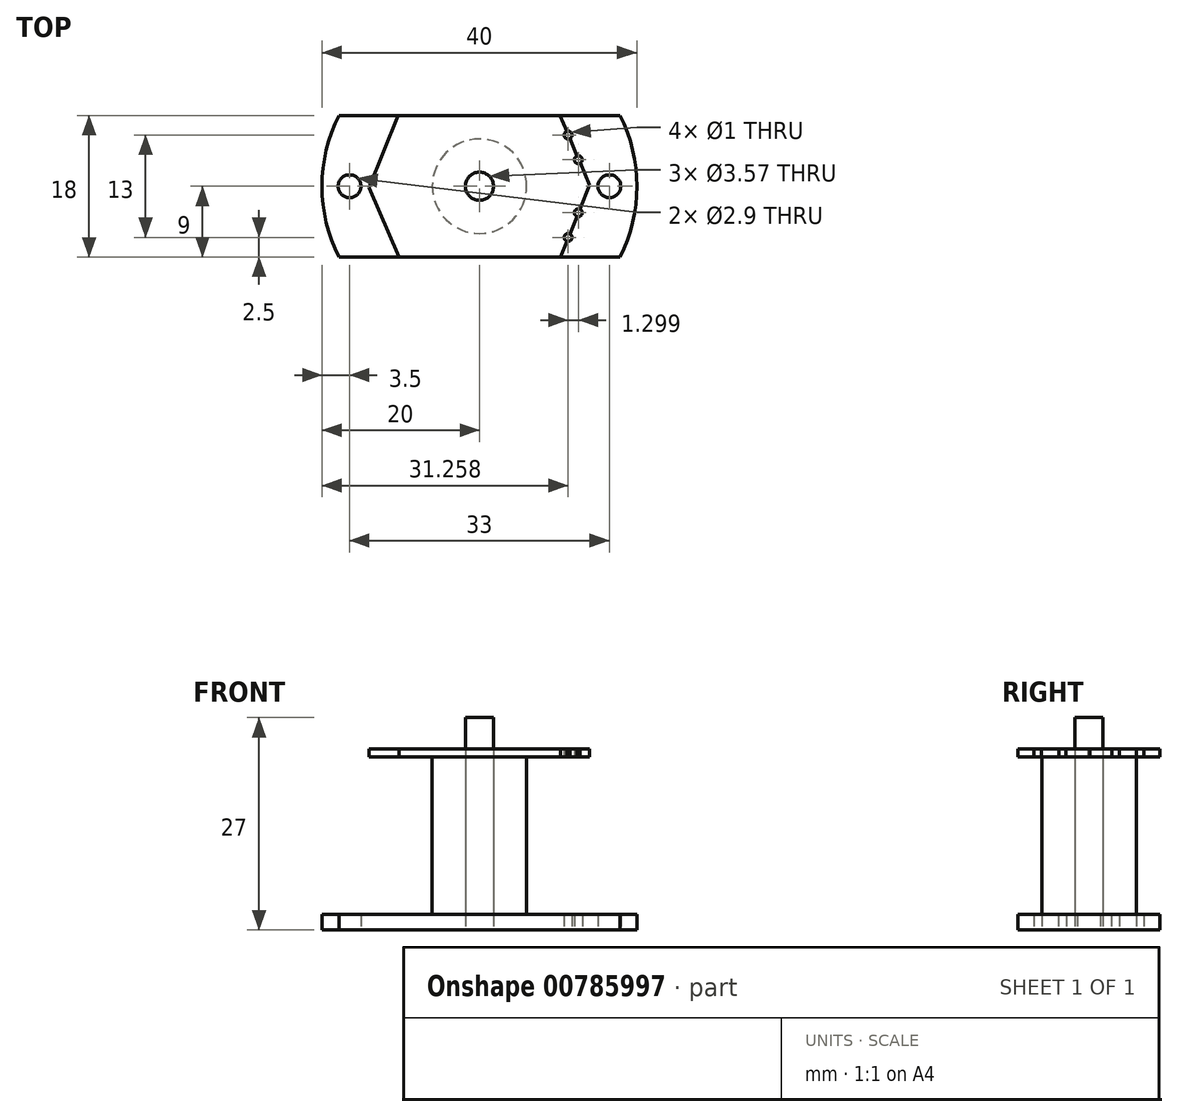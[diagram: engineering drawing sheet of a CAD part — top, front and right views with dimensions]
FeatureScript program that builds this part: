
annotation { "Feature Type Name" : "Feature", "Feature Type Description" : "" }
export const myFeature = defineFeature(function(context is Context, id is Id, definition is map)
    precondition{}
    {
        {
            var Q0;
            Q0=qCreatedBy(makeId("Top.planeOp"),FACE);
            var sketch = newSketch(context, id + "F0", { "sketchPlane" : qUnion([Q0])});
            skCircle(sketch, "E0", {"center": v(0, 0) * mm, "radius": 20 * mm});
            skCircle(sketch, "E1", {"center": v(-16.5, 0) * mm, "radius": 1.45 * mm});
            skCircle(sketch, "E2", {"center": v(16.5, 0) * mm, "radius": 1.45 * mm});
            skCircle(sketch, "E3", {"center": v(0, 0) * mm, "radius": 1.79 * mm});
            skLineSegment(sketch, "E4", {"start": v(0, 14.44) * mm, "end": v(0, -15.2) * mm, "construction": true});
            skSolve(sketch);
        }
        {
            var Q0;
            Q0=qSketchRegion(id+"F0",true);
            extrude(context, id + "F1", {"entities" : qUnion([Q0]), "depth" : 2 * mm, "offsetDistance" : 25 * mm});
        }
        {
            var Q0;
            Q0=makeQuery(id+"F1.opExtrude","CAP_FACE",FACE,{"disambiguationData":[OSD([sQuery(id+"F0.wireOp",EDGE,"E0"),sQuery(id+"F0.wireOp",EDGE,"E1"),sQuery(id+"F0.wireOp",EDGE,"E2"),sQuery(id+"F0.wireOp",EDGE,"E3")])],"isStart":false});
            var sketch = newSketch(context, id + "F2", { "sketchPlane" : qUnion([Q0])});
            skCircle(sketch, "E5", {"center": v(0, 0) * mm, "radius": 1.79 * mm});
            skCircle(sketch, "E6", {"center": v(0, 0) * mm, "radius": 6 * mm});
            skSolve(sketch);
        }
        {
            var Q0;
            Q0=qSketchRegion(id+"F2",true);
            extrude(context, id + "F3", {"entities" : qUnion([Q0]), "depth" : 20 * mm, "offsetDistance" : 25 * mm});
        }
        {
            var Q0;
            Q0=makeQuery(id+"F1.opExtrude","CAP_FACE",FACE,{"disambiguationData":[OSD([sQuery(id+"F0.wireOp",EDGE,"E0"),sQuery(id+"F0.wireOp",EDGE,"E1"),sQuery(id+"F0.wireOp",EDGE,"E2"),sQuery(id+"F0.wireOp",EDGE,"E3")])],"isStart":true});
            var sketch = newSketch(context, id + "F4", { "sketchPlane" : qUnion([Q0])});
            skCircle(sketch, "E7", {"center": v(0, 0) * mm, "radius": 1.79 * mm});
            skSolve(sketch);
        }
        {
            var Q0;
            Q0=qSketchRegion(id+"F4",true);
            extrude(context, id + "F5", {"entities" : qUnion([Q0]), "oppositeDirection" : true, "depth" : 20 * mm + 6 * mm + 1 * mm, "offsetDistance" : 25 * mm});
        }
        {
            var Q0;
            Q0=makeQuery(id+"F3.opExtrude","CAP_FACE",FACE,{"disambiguationData":[OSD([sQuery(id+"F2.wireOp",EDGE,"E5"),sQuery(id+"F2.wireOp",EDGE,"E6")])],"isStart":false});
            var sketch = newSketch(context, id + "F6", { "sketchPlane" : qUnion([Q0])});
            skCircle(sketch, "E8.cCircle", {"center": v(0, 0) * mm, "radius": 14 * mm, "construction": true});
            skLineSegment(sketch, "E8.0", {"start": v(-10, 9.8) * mm, "end": v(-0.14, 14) * mm});
            skLineSegment(sketch, "E8.1", {"start": v(-0.14, 14) * mm, "end": v(9.8, 10) * mm});
            skLineSegment(sketch, "E8.2", {"start": v(9.8, 10) * mm, "end": v(14, 0.14) * mm});
            skLineSegment(sketch, "E8.3", {"start": v(14, 0.14) * mm, "end": v(10, -9.8) * mm});
            skLineSegment(sketch, "E8.4", {"start": v(10, -9.8) * mm, "end": v(0.14, -14) * mm});
            skLineSegment(sketch, "E8.5", {"start": v(0.14, -14) * mm, "end": v(-9.8, -10) * mm});
            skLineSegment(sketch, "E8.6", {"start": v(-9.8, -10) * mm, "end": v(-14, -0.14) * mm});
            skLineSegment(sketch, "E8.7", {"start": v(-14, -0.14) * mm, "end": v(-10, 9.8) * mm});
            skLineSegment(sketch, "E9", {"start": v(0, 13.2) * mm, "end": v(0, -15.16) * mm, "construction": true});
            skCircle(sketch, "E10", {"center": v(0, 0) * mm, "radius": 1.79 * mm});
            skSolve(sketch);
        }
        {
            var Q0;
            Q0=qSketchRegion(id+"F6",true);
            extrude(context, id + "F7", {"entities" : qUnion([Q0]), "depth" : 1 * mm, "offsetDistance" : 25 * mm});
        }
        {
            var Q0;
            Q0=makeQuery(id+"F1.opExtrude","CAP_FACE",FACE,{"disambiguationData":[OSD([sQuery(id+"F0.wireOp",EDGE,"E0"),sQuery(id+"F0.wireOp",EDGE,"E1"),sQuery(id+"F0.wireOp",EDGE,"E2"),sQuery(id+"F0.wireOp",EDGE,"E3")])],"isStart":true});
            var sketch = newSketch(context, id + "F8", { "sketchPlane" : qUnion([Q0])});
            skLineSegment(sketch, "E11.bottom", {"start": v(-25, -9) * mm, "end": v(25, -9) * mm});
            skLineSegment(sketch, "E11.top", {"start": v(-25, 9) * mm, "end": v(25, 9) * mm});
            skLineSegment(sketch, "E11.left", {"start": v(-25, -9) * mm, "end": v(-25, 9) * mm});
            skLineSegment(sketch, "E11.right", {"start": v(25, -9) * mm, "end": v(25, 9) * mm});
            skPoint(sketch, "E11.middle", {"position": v(0, 0) * mm});
            skCircle(sketch, "E12", {"center": v(0, 0) * mm, "radius": 26.57 * mm});
            skSolve(sketch);
        }
        {
            var Q0;
            {var subQ0=sQuery(id+"F8.wireOp",EDGE,"E11.top");var subQ1=makeQuery(id+"F1.opExtrude","CAP_EDGE",EDGE,{"disambiguationData":[OSD([sQuery(id+"F0.wireOp",EDGE,"E0")])],"isStart":true});var subQ2=makeQuery(id+"F8.imprint","INTERSECT",VERTEX,{"disambiguationData":[OD(0.0)],"derivedFrom":[subQ1,subQ0]});Q0=makeQuery(id+"F8.imprint","IMPRINT",FACE,{"disambiguationData":[TD([[makeQuery(id+"F8.imprint","IMPRINT",EDGE,{"disambiguationData":[TD([[subQ2,-1.0]])],"derivedFrom":subQ0}),1.0]])]});}
            var Q1;
            {var subQ0=sQuery(id+"F8.wireOp",EDGE,"E11.bottom");var subQ1=makeQuery(id+"F1.opExtrude","CAP_EDGE",EDGE,{"disambiguationData":[OSD([sQuery(id+"F0.wireOp",EDGE,"E0")])],"isStart":true});var subQ2=makeQuery(id+"F8.imprint","INTERSECT",VERTEX,{"disambiguationData":[OD(0.0)],"derivedFrom":[subQ1,subQ0]});Q1=makeQuery(id+"F8.imprint","IMPRINT",FACE,{"disambiguationData":[TD([[makeQuery(id+"F8.imprint","IMPRINT",EDGE,{"disambiguationData":[TD([[subQ2,-1.0]])],"derivedFrom":subQ0}),-1.0]])]});}
            extrude(context, id + "F9", {"entities" : qUnion([Q0, Q1]), "operationType" : NewBodyOperationType.REMOVE, "oppositeDirection" : true, "depth" : 25 * mm, "offsetDistance" : 25 * mm});
        }
        {
            var Q0;
            Q0=makeQuery(id+"F1.opExtrude","CAP_FACE",FACE,{"disambiguationData":[OSD([sQuery(id+"F0.wireOp",EDGE,"E0"),sQuery(id+"F0.wireOp",EDGE,"E1"),sQuery(id+"F0.wireOp",EDGE,"E2"),sQuery(id+"F0.wireOp",EDGE,"E3")])],"isStart":true});
            var sketch = newSketch(context, id + "F10", { "sketchPlane" : qUnion([Q0])});
            skCircle(sketch, "E13", {"center": v(11.26, 6.5) * mm, "radius": 0.5 * mm});
            skCircle(sketch, "E14", {"center": v(12.56, 3.36) * mm, "radius": 0.5 * mm});
            skLineSegment(sketch, "E15", {"start": v(0, 0) * mm, "end": v(11.26, 6.5) * mm, "construction": true});
            skLineSegment(sketch, "E16", {"start": v(0, 0) * mm, "end": v(12.56, 3.36) * mm, "construction": true});
            skCircle(sketch, "E17.MirrorC", {"center": v(12.56, -3.36) * mm, "radius": 0.5 * mm});
            skCircle(sketch, "E18.MirrorC", {"center": v(11.26, -6.5) * mm, "radius": 0.5 * mm});
            skSolve(sketch);
        }
        {
            var Q0;
            Q0=qSketchRegion(id+"F10",true);
            extrude(context, id + "F11", {"entities" : qUnion([Q0]), "operationType" : NewBodyOperationType.REMOVE, "oppositeDirection" : true, "depth" : 25 * mm, "offsetDistance" : 25 * mm});
        }
    });
